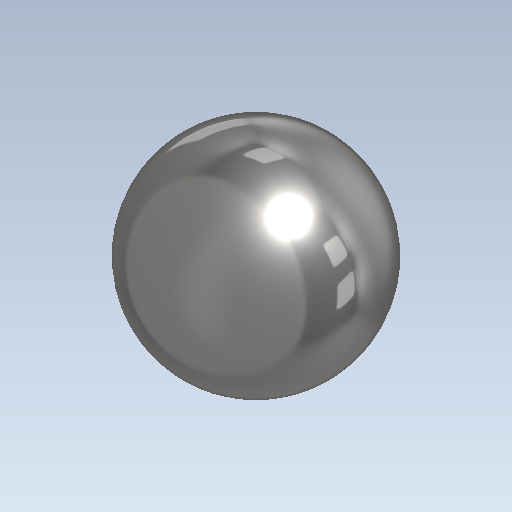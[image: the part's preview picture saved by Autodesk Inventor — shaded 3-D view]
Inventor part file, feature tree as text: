
AUTODESK INVENTOR PART (.ipt)
format: ipt  version: 2020.3 (Build 243373000, 373)  size: 150,528 bytes
history: native  units: mm (DEFAULTED — no unit token found)
features: other x7, revolve x1, sketch x1
ambient origin geometry x8: Origin, YZ Plane, XZ Plane, XY Plane, X Axis, Y Axis, Z Axis, Center Point
bodies: Solid1 (feature_tree)
feature tree (9):
  revolve  "Revolution1"  [1 undecoded]
  other  "ip_st_1_XY"
  other  "ip_st_1_YZ"
  other  "ip_st_1_ZX"
  other  "ip_st_1_X"
  other  "ip_st_1_Y"
  other  "ip_st_1_Z"
  other  "ip_st_1_Center"
  sketch  "Sketch_1"  dims[d0=360.0deg]
note: 1 required parameter value undecoded (feature->parameter linkage not recoverable at this tier; creation-order binding heuristic only, values carry confidence <= 0.55)
